# Revit family: 815969
name_source: partatom
category: Specialty Equipment
units: mm (PartAtom-declared; Revit-internal decimal feet)

## family parameters
Cut with Voids When Loaded = No
Host = Face
OmniClass Number = 23.40.20.21.17
OmniClass Title = Paper Towel Dispensers, Disposal Units
Part Type = Normal
Room Calculation Point = No
Round Connector Dimension = Use Diameter
Shared = Yes

## types (1)
- 815969
    ADA Compliant = Yes
    ATS URL = http://www.atsspec.net
    Assembly Code = E1090900
    Cabinet Depth = 143 mm
    Default Elevation = 2032 mm
    Description = Bobrick TrimLineSeries™ Recessed Paper Towel Dispenser, Automatic Hand Dryer, and Waste Receptacle (3-in-1 unit)
    Door Thickness = 14 mm  [stored 0.0459318 ft]
    Finish = Stainless Steel-Bobrick-Type 304-Satin
    Height = 1829 mm  [stored 6.00066 ft]
    Installation Type = Recessed in Wall
    Manufacturer = Bobrick
    Materials = Stainless Steel-Bobrick-Type 304-Satin
    Model = 815969
    Omniclass Table 23 Code = 23.40.20.21.17
    Omniclass Table 23 Title = Paper Towel Dispenser, Disposal Units
    Product Documentation Link = https://www.bobrick.com
    Product URL = https://www.bobrick.com
    Type Comments = Automatic Hand Dryer: 220-240V AC, 7 Amp, 1500-1700 Watts, 50/60 Hz, Single Phase, VDE approved, CE marked.
    URL = http://www.bobrick.com
    Warranty Documentation Link = https://www.bobrick.com
    Warranty Information = 1 Year Limited Warranty
    Width = 330 mm

note: [stored X ft] marks values corroborated as IEEE doubles in the binary element streams (Revit-internal decimal feet)

## geometry (parser evidence)
native form markers: Sweep x3
no freeform markers — native parametric forms only
